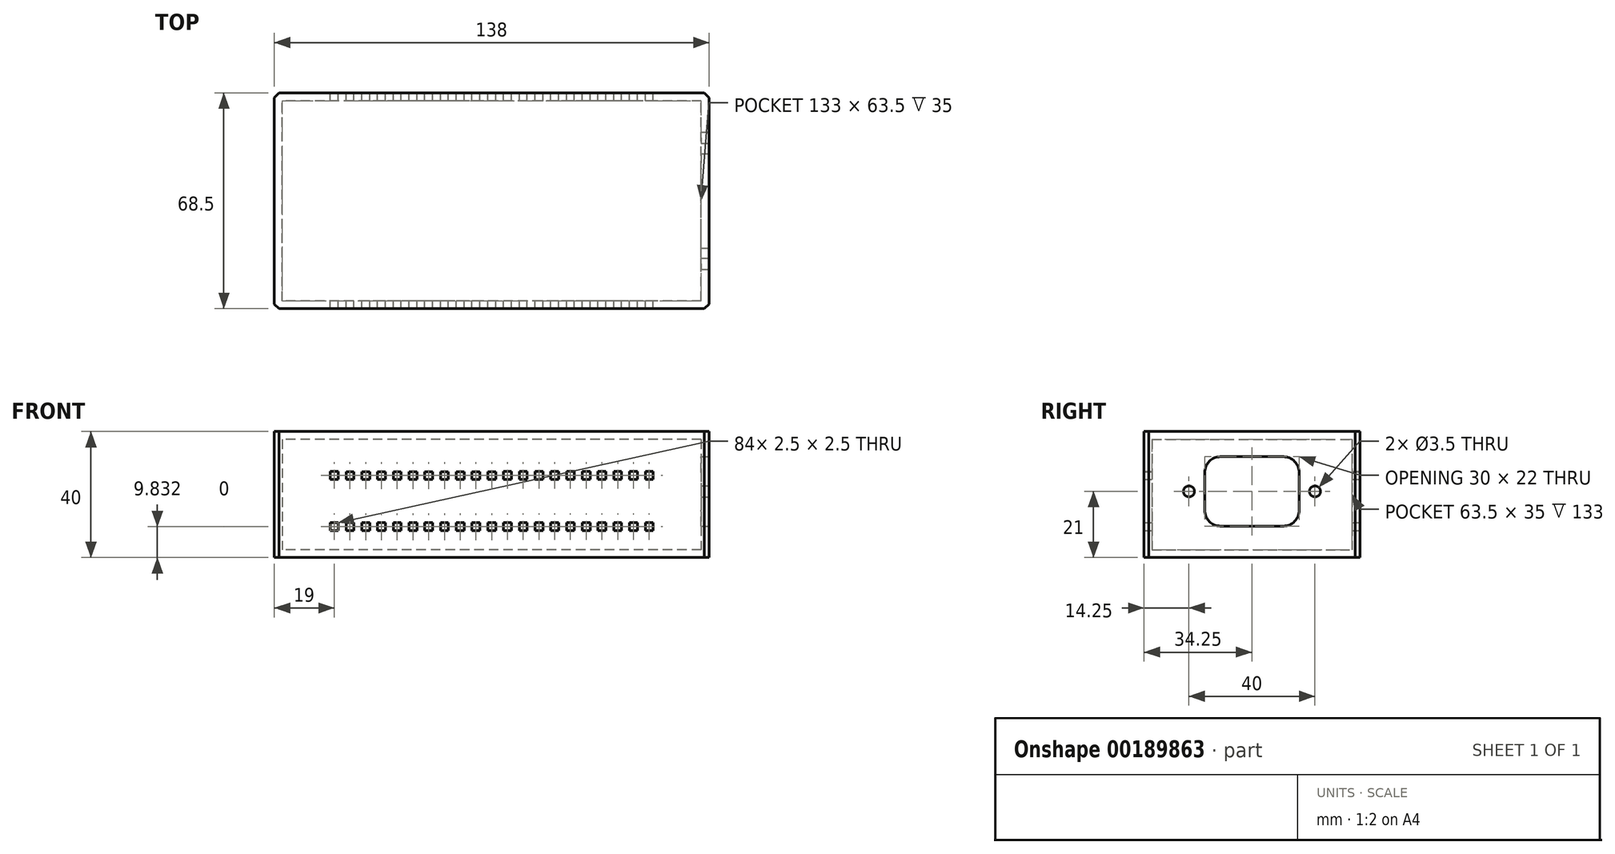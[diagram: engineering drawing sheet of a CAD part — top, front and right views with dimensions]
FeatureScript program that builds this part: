
annotation { "Feature Type Name" : "Feature", "Feature Type Description" : "" }
export const myFeature = defineFeature(function(context is Context, id is Id, definition is map)
    precondition{}
    {
        {
            var Q0;
            Q0=qCreatedBy(makeId("Top.planeOp"),FACE);
            var sketch = newSketch(context, id + "F0", { "sketchPlane" : qUnion([Q0])});
            skLineSegment(sketch, "E0.bottom", {"start": v(69, -34.25) * mm, "end": v(-69, -34.25) * mm});
            skLineSegment(sketch, "E0.top", {"start": v(69, 34.25) * mm, "end": v(-69, 34.25) * mm});
            skLineSegment(sketch, "E0.left", {"start": v(69, -34.25) * mm, "end": v(69, 34.25) * mm});
            skLineSegment(sketch, "E0.right", {"start": v(-69, -34.25) * mm, "end": v(-69, 34.25) * mm});
            skPoint(sketch, "E0.middle", {"position": v(0, 0) * mm});
            skSolve(sketch);
        }
        {
            var Q0;
            Q0 = qSketchRegion(id + "F0", true);
            extrude(context, id + "F1", {"entities" : qUnion([Q0]), "depth" : 40 * mm});
        }
        {
            var Q0;
            Q0=makeQuery(id+"F1.opExtrude","CAP_FACE",FACE,{"disambiguationData":[OSD([sQuery(id+"F0.wireOp",EDGE,"E0.bottom"),sQuery(id+"F0.wireOp",EDGE,"E0.top"),sQuery(id+"F0.wireOp",EDGE,"E0.left"),sQuery(id+"F0.wireOp",EDGE,"E0.right")])],"isStart":false});
            var Q1;
            Q1=makeQuery(id+"F1.opExtrude","SWEPT_BODY",BODY,{"disambiguationData":[OSD([sQuery(id+"F0.wireOp",EDGE,"E0.bottom"),sQuery(id+"F0.wireOp",EDGE,"E0.top"),sQuery(id+"F0.wireOp",EDGE,"E0.left"),sQuery(id+"F0.wireOp",EDGE,"E0.right")])]});
            shell(context, id + "F2", {"isHollow" : true, "entities" : qUnion([Q0]), "parts" : qUnion([Q1]), "thickness" : 2.5 * mm});
        }
        {
            var Q0;
            Q0=makeQuery(id+"F1.opExtrude","SWEPT_EDGE",EDGE,{"disambiguationData":[OSD([sQuery(id+"F0.wireOp",EDGE,"E0.top"),sQuery(id+"F0.wireOp",EDGE,"E0.right")])]});
            var Q1;
            Q1=makeQuery(id+"F1.opExtrude","SWEPT_EDGE",EDGE,{"disambiguationData":[OSD([sQuery(id+"F0.wireOp",EDGE,"E0.bottom"),sQuery(id+"F0.wireOp",EDGE,"E0.right")])]});
            var Q2;
            Q2=makeQuery(id+"F1.opExtrude","SWEPT_EDGE",EDGE,{"disambiguationData":[OSD([sQuery(id+"F0.wireOp",EDGE,"E0.top"),sQuery(id+"F0.wireOp",EDGE,"E0.left")])]});
            var Q3;
            Q3=makeQuery(id+"F1.opExtrude","SWEPT_EDGE",EDGE,{"disambiguationData":[OSD([sQuery(id+"F0.wireOp",EDGE,"E0.bottom"),sQuery(id+"F0.wireOp",EDGE,"E0.left")])]});
            chamfer(context, id + "F3", {"entities" : qUnion([Q0, Q1, Q2, Q3]), "width" : 1.5 * mm, "tangentPropagation" : true});
        }
        {
            var Q0;
            Q0=makeQuery(id+"F1.opExtrude","SWEPT_FACE",FACE,{"disambiguationData":[OSD([sQuery(id+"F0.wireOp",EDGE,"E0.left")])]});
            var sketch = newSketch(context, id + "F4", { "sketchPlane" : qUnion([Q0])});
            skLineSegment(sketch, "E1.bottom", {"start": v(15, 10) * mm, "end": v(-15, 10) * mm});
            skLineSegment(sketch, "E1.top", {"start": v(15, 32) * mm, "end": v(-15, 32) * mm});
            skLineSegment(sketch, "E1.left", {"start": v(15, 10) * mm, "end": v(15, 32) * mm});
            skLineSegment(sketch, "E1.right", {"start": v(-15, 10) * mm, "end": v(-15, 32) * mm});
            skPoint(sketch, "E1.middle", {"position": v(0, 21) * mm});
            skCircle(sketch, "E2", {"center": v(-20, 21) * mm, "radius": 1.75 * mm});
            skCircle(sketch, "E3", {"center": v(20, 21) * mm, "radius": 1.75 * mm});
            skSolve(sketch);
        }
        {
            var Q0;
            Q0 = qSketchRegion(id + "F4", true);
            extrude(context, id + "F5", {"entities" : qUnion([Q0]), "operationType" : NewBodyOperationType.REMOVE, "oppositeDirection" : true, "depth" : 25 * mm});
        }
        {
            var Q0;
            Q0=makeQuery(id+"F5.boolean.opBoolean","COPY",EDGE,{"derivedFrom":makeQuery(id+"F5.opExtrude","SWEPT_EDGE",EDGE,{"disambiguationData":[OSD([sQuery(id+"F4.wireOp",EDGE,"E1.bottom"),sQuery(id+"F4.wireOp",EDGE,"E1.right")])]})});
            var Q1;
            Q1=makeQuery(id+"F5.boolean.opBoolean","COPY",EDGE,{"derivedFrom":makeQuery(id+"F5.opExtrude","SWEPT_EDGE",EDGE,{"disambiguationData":[OSD([sQuery(id+"F4.wireOp",EDGE,"E1.bottom"),sQuery(id+"F4.wireOp",EDGE,"E1.left")])]})});
            var Q2;
            Q2=makeQuery(id+"F5.boolean.opBoolean","COPY",EDGE,{"derivedFrom":makeQuery(id+"F5.opExtrude","SWEPT_EDGE",EDGE,{"disambiguationData":[OSD([sQuery(id+"F4.wireOp",EDGE,"E1.top"),sQuery(id+"F4.wireOp",EDGE,"E1.left")])]})});
            var Q3;
            Q3=makeQuery(id+"F5.boolean.opBoolean","COPY",EDGE,{"derivedFrom":makeQuery(id+"F5.opExtrude","SWEPT_EDGE",EDGE,{"disambiguationData":[OSD([sQuery(id+"F4.wireOp",EDGE,"E1.top"),sQuery(id+"F4.wireOp",EDGE,"E1.right")])]})});
            fillet(context, id + "F6", {"entities" : qUnion([Q0, Q1, Q2, Q3]), "radius" : 5 * mm, "tangentPropagation" : true, "allowEdgeOverflow" : false});
        }
        {
            var Q0;
            Q0=makeQuery(id+"F1.opExtrude","SWEPT_FACE",FACE,{"disambiguationData":[OSD([sQuery(id+"F0.wireOp",EDGE,"E0.top")])]});
            var sketch = newSketch(context, id + "F7", { "sketchPlane" : qUnion([Q0])});
            skLineSegment(sketch, "E4.bottom", {"start": v(1.25, 24.8) * mm, "end": v(-1.25, 24.8) * mm});
            skLineSegment(sketch, "E4.top", {"start": v(1.25, 27.3) * mm, "end": v(-1.25, 27.3) * mm});
            skLineSegment(sketch, "E4.left", {"start": v(1.25, 24.8) * mm, "end": v(1.25, 27.3) * mm});
            skLineSegment(sketch, "E4.right", {"start": v(-1.25, 24.8) * mm, "end": v(-1.25, 27.3) * mm});
            skPoint(sketch, "E4.middle", {"position": v(0, 26.04) * mm});
            skLineSegment(sketch, "E5.1.0.0", {"start": v(6.25, 27.3) * mm, "end": v(3.75, 27.3) * mm});
            skLineSegment(sketch, "E5.1.0.1", {"start": v(3.75, 24.8) * mm, "end": v(3.75, 27.3) * mm});
            skPoint(sketch, "E5.1.0.2", {"position": v(5, 26.04) * mm});
            skLineSegment(sketch, "E5.1.0.3", {"start": v(6.25, 24.8) * mm, "end": v(6.25, 27.3) * mm});
            skLineSegment(sketch, "E5.1.0.4", {"start": v(6.25, 24.8) * mm, "end": v(3.75, 24.8) * mm});
            skLineSegment(sketch, "E5.2.0.0", {"start": v(11.25, 27.3) * mm, "end": v(8.75, 27.3) * mm});
            skLineSegment(sketch, "E5.2.0.1", {"start": v(8.75, 24.8) * mm, "end": v(8.75, 27.3) * mm});
            skPoint(sketch, "E5.2.0.2", {"position": v(10, 26.04) * mm});
            skLineSegment(sketch, "E5.2.0.3", {"start": v(11.25, 24.8) * mm, "end": v(11.25, 27.3) * mm});
            skLineSegment(sketch, "E5.2.0.4", {"start": v(11.25, 24.8) * mm, "end": v(8.75, 24.8) * mm});
            skLineSegment(sketch, "E5.3.0.0", {"start": v(16.25, 27.3) * mm, "end": v(13.75, 27.3) * mm});
            skLineSegment(sketch, "E5.3.0.1", {"start": v(13.75, 24.8) * mm, "end": v(13.75, 27.3) * mm});
            skPoint(sketch, "E5.3.0.2", {"position": v(15, 26.04) * mm});
            skLineSegment(sketch, "E5.3.0.3", {"start": v(16.25, 24.8) * mm, "end": v(16.25, 27.3) * mm});
            skLineSegment(sketch, "E5.3.0.4", {"start": v(16.25, 24.8) * mm, "end": v(13.75, 24.8) * mm});
            skLineSegment(sketch, "E5.4.0.0", {"start": v(21.25, 27.3) * mm, "end": v(18.75, 27.3) * mm});
            skLineSegment(sketch, "E5.4.0.1", {"start": v(18.75, 24.8) * mm, "end": v(18.75, 27.3) * mm});
            skPoint(sketch, "E5.4.0.2", {"position": v(20, 26.04) * mm});
            skLineSegment(sketch, "E5.4.0.3", {"start": v(21.25, 24.8) * mm, "end": v(21.25, 27.3) * mm});
            skLineSegment(sketch, "E5.4.0.4", {"start": v(21.25, 24.8) * mm, "end": v(18.75, 24.8) * mm});
            skLineSegment(sketch, "E5.5.0.0", {"start": v(26.25, 27.3) * mm, "end": v(23.75, 27.3) * mm});
            skLineSegment(sketch, "E5.5.0.1", {"start": v(23.75, 24.8) * mm, "end": v(23.75, 27.3) * mm});
            skPoint(sketch, "E5.5.0.2", {"position": v(25, 26.04) * mm});
            skLineSegment(sketch, "E5.5.0.3", {"start": v(26.25, 24.8) * mm, "end": v(26.25, 27.3) * mm});
            skLineSegment(sketch, "E5.5.0.4", {"start": v(26.25, 24.8) * mm, "end": v(23.75, 24.8) * mm});
            skLineSegment(sketch, "E5.6.0.0", {"start": v(31.25, 27.3) * mm, "end": v(28.75, 27.3) * mm});
            skLineSegment(sketch, "E5.6.0.1", {"start": v(28.75, 24.8) * mm, "end": v(28.75, 27.3) * mm});
            skPoint(sketch, "E5.6.0.2", {"position": v(30, 26.04) * mm});
            skLineSegment(sketch, "E5.6.0.3", {"start": v(31.25, 24.8) * mm, "end": v(31.25, 27.3) * mm});
            skLineSegment(sketch, "E5.6.0.4", {"start": v(31.25, 24.8) * mm, "end": v(28.75, 24.8) * mm});
            skLineSegment(sketch, "E5.7.0.0", {"start": v(36.25, 27.3) * mm, "end": v(33.75, 27.3) * mm});
            skLineSegment(sketch, "E5.7.0.1", {"start": v(33.75, 24.8) * mm, "end": v(33.75, 27.3) * mm});
            skPoint(sketch, "E5.7.0.2", {"position": v(35, 26.04) * mm});
            skLineSegment(sketch, "E5.7.0.3", {"start": v(36.25, 24.8) * mm, "end": v(36.25, 27.3) * mm});
            skLineSegment(sketch, "E5.7.0.4", {"start": v(36.25, 24.8) * mm, "end": v(33.75, 24.8) * mm});
            skLineSegment(sketch, "E5.8.0.0", {"start": v(41.25, 27.3) * mm, "end": v(38.75, 27.3) * mm});
            skLineSegment(sketch, "E5.8.0.1", {"start": v(38.75, 24.8) * mm, "end": v(38.75, 27.3) * mm});
            skPoint(sketch, "E5.8.0.2", {"position": v(40, 26.04) * mm});
            skLineSegment(sketch, "E5.8.0.3", {"start": v(41.25, 24.8) * mm, "end": v(41.25, 27.3) * mm});
            skLineSegment(sketch, "E5.8.0.4", {"start": v(41.25, 24.8) * mm, "end": v(38.75, 24.8) * mm});
            skLineSegment(sketch, "E5.9.0.0", {"start": v(46.25, 27.3) * mm, "end": v(43.75, 27.3) * mm});
            skLineSegment(sketch, "E5.9.0.1", {"start": v(43.75, 24.8) * mm, "end": v(43.75, 27.3) * mm});
            skPoint(sketch, "E5.9.0.2", {"position": v(45, 26.04) * mm});
            skLineSegment(sketch, "E5.9.0.3", {"start": v(46.25, 24.8) * mm, "end": v(46.25, 27.3) * mm});
            skLineSegment(sketch, "E5.9.0.4", {"start": v(46.25, 24.8) * mm, "end": v(43.75, 24.8) * mm});
            skLineSegment(sketch, "E5.direction1", {"start": v(-1.25, 24.8) * mm, "end": v(3.75, 24.8) * mm, "construction": true});
            skLineSegment(sketch, "E6.bottom", {"start": v(-48.75, 24.83) * mm, "end": v(-51.25, 24.83) * mm});
            skLineSegment(sketch, "E6.top", {"start": v(-48.75, 27.33) * mm, "end": v(-51.25, 27.33) * mm});
            skLineSegment(sketch, "E6.left", {"start": v(-48.75, 24.83) * mm, "end": v(-48.75, 27.33) * mm});
            skLineSegment(sketch, "E6.right", {"start": v(-51.25, 24.83) * mm, "end": v(-51.25, 27.33) * mm});
            skPoint(sketch, "E6.middle", {"position": v(-50, 26.08) * mm});
            skLineSegment(sketch, "E7.1.0.0", {"start": v(-43.75, 27.33) * mm, "end": v(-46.25, 27.33) * mm});
            skLineSegment(sketch, "E7.1.0.1", {"start": v(-46.25, 24.83) * mm, "end": v(-46.25, 27.33) * mm});
            skPoint(sketch, "E7.1.0.2", {"position": v(-45, 26.08) * mm});
            skLineSegment(sketch, "E7.1.0.3", {"start": v(-43.75, 24.83) * mm, "end": v(-43.75, 27.33) * mm});
            skLineSegment(sketch, "E7.1.0.4", {"start": v(-43.75, 24.83) * mm, "end": v(-46.25, 24.83) * mm});
            skLineSegment(sketch, "E7.2.0.0", {"start": v(-38.75, 27.33) * mm, "end": v(-41.25, 27.33) * mm});
            skLineSegment(sketch, "E7.2.0.1", {"start": v(-41.25, 24.83) * mm, "end": v(-41.25, 27.33) * mm});
            skPoint(sketch, "E7.2.0.2", {"position": v(-40, 26.08) * mm});
            skLineSegment(sketch, "E7.2.0.3", {"start": v(-38.75, 24.83) * mm, "end": v(-38.75, 27.33) * mm});
            skLineSegment(sketch, "E7.2.0.4", {"start": v(-38.75, 24.83) * mm, "end": v(-41.25, 24.83) * mm});
            skLineSegment(sketch, "E7.3.0.0", {"start": v(-33.75, 27.33) * mm, "end": v(-36.25, 27.33) * mm});
            skLineSegment(sketch, "E7.3.0.1", {"start": v(-36.25, 24.83) * mm, "end": v(-36.25, 27.33) * mm});
            skPoint(sketch, "E7.3.0.2", {"position": v(-35, 26.08) * mm});
            skLineSegment(sketch, "E7.3.0.3", {"start": v(-33.75, 24.83) * mm, "end": v(-33.75, 27.33) * mm});
            skLineSegment(sketch, "E7.3.0.4", {"start": v(-33.75, 24.83) * mm, "end": v(-36.25, 24.83) * mm});
            skLineSegment(sketch, "E7.4.0.0", {"start": v(-28.75, 27.33) * mm, "end": v(-31.25, 27.33) * mm});
            skLineSegment(sketch, "E7.4.0.1", {"start": v(-31.25, 24.83) * mm, "end": v(-31.25, 27.33) * mm});
            skPoint(sketch, "E7.4.0.2", {"position": v(-30, 26.08) * mm});
            skLineSegment(sketch, "E7.4.0.3", {"start": v(-28.75, 24.83) * mm, "end": v(-28.75, 27.33) * mm});
            skLineSegment(sketch, "E7.4.0.4", {"start": v(-28.75, 24.83) * mm, "end": v(-31.25, 24.83) * mm});
            skLineSegment(sketch, "E7.5.0.0", {"start": v(-23.75, 27.33) * mm, "end": v(-26.25, 27.33) * mm});
            skLineSegment(sketch, "E7.5.0.1", {"start": v(-26.25, 24.83) * mm, "end": v(-26.25, 27.33) * mm});
            skPoint(sketch, "E7.5.0.2", {"position": v(-25, 26.08) * mm});
            skLineSegment(sketch, "E7.5.0.3", {"start": v(-23.75, 24.83) * mm, "end": v(-23.75, 27.33) * mm});
            skLineSegment(sketch, "E7.5.0.4", {"start": v(-23.75, 24.83) * mm, "end": v(-26.25, 24.83) * mm});
            skLineSegment(sketch, "E7.6.0.0", {"start": v(-18.75, 27.33) * mm, "end": v(-21.25, 27.33) * mm});
            skLineSegment(sketch, "E7.6.0.1", {"start": v(-21.25, 24.83) * mm, "end": v(-21.25, 27.33) * mm});
            skPoint(sketch, "E7.6.0.2", {"position": v(-20, 26.08) * mm});
            skLineSegment(sketch, "E7.6.0.3", {"start": v(-18.75, 24.83) * mm, "end": v(-18.75, 27.33) * mm});
            skLineSegment(sketch, "E7.6.0.4", {"start": v(-18.75, 24.83) * mm, "end": v(-21.25, 24.83) * mm});
            skLineSegment(sketch, "E7.7.0.0", {"start": v(-13.75, 27.33) * mm, "end": v(-16.25, 27.33) * mm});
            skLineSegment(sketch, "E7.7.0.1", {"start": v(-16.25, 24.83) * mm, "end": v(-16.25, 27.33) * mm});
            skPoint(sketch, "E7.7.0.2", {"position": v(-15, 26.08) * mm});
            skLineSegment(sketch, "E7.7.0.3", {"start": v(-13.75, 24.83) * mm, "end": v(-13.75, 27.33) * mm});
            skLineSegment(sketch, "E7.7.0.4", {"start": v(-13.75, 24.83) * mm, "end": v(-16.25, 24.83) * mm});
            skLineSegment(sketch, "E7.8.0.0", {"start": v(-8.75, 27.33) * mm, "end": v(-11.25, 27.33) * mm});
            skLineSegment(sketch, "E7.8.0.1", {"start": v(-11.25, 24.83) * mm, "end": v(-11.25, 27.33) * mm});
            skPoint(sketch, "E7.8.0.2", {"position": v(-10, 26.08) * mm});
            skLineSegment(sketch, "E7.8.0.3", {"start": v(-8.75, 24.83) * mm, "end": v(-8.75, 27.33) * mm});
            skLineSegment(sketch, "E7.8.0.4", {"start": v(-8.75, 24.83) * mm, "end": v(-11.25, 24.83) * mm});
            skLineSegment(sketch, "E7.9.0.0", {"start": v(-3.75, 27.33) * mm, "end": v(-6.25, 27.33) * mm});
            skLineSegment(sketch, "E7.9.0.1", {"start": v(-6.25, 24.83) * mm, "end": v(-6.25, 27.33) * mm});
            skPoint(sketch, "E7.9.0.2", {"position": v(-5, 26.08) * mm});
            skLineSegment(sketch, "E7.9.0.3", {"start": v(-3.75, 24.83) * mm, "end": v(-3.75, 27.33) * mm});
            skLineSegment(sketch, "E7.9.0.4", {"start": v(-3.75, 24.83) * mm, "end": v(-6.25, 24.83) * mm});
            skLineSegment(sketch, "E7.direction1", {"start": v(-51.25, 24.83) * mm, "end": v(-46.25, 24.83) * mm, "construction": true});
            skLineSegment(sketch, "E8.9.0.0", {"start": v(51.25, 27.33) * mm, "end": v(48.75, 27.33) * mm});
            skLineSegment(sketch, "E8.9.0.1", {"start": v(48.75, 24.83) * mm, "end": v(48.75, 27.33) * mm});
            skPoint(sketch, "E8.9.0.2", {"position": v(50, 26.08) * mm});
            skLineSegment(sketch, "E8.9.0.3", {"start": v(51.25, 24.83) * mm, "end": v(51.25, 27.33) * mm});
            skLineSegment(sketch, "E8.9.0.4", {"start": v(51.25, 24.83) * mm, "end": v(48.75, 24.83) * mm});
            skLineSegment(sketch, "E9.bottom", {"start": v(1.25, 8.54) * mm, "end": v(-1.25, 8.54) * mm});
            skLineSegment(sketch, "E9.top", {"start": v(1.25, 11.04) * mm, "end": v(-1.25, 11.04) * mm});
            skLineSegment(sketch, "E9.left", {"start": v(1.25, 8.54) * mm, "end": v(1.25, 11.04) * mm});
            skLineSegment(sketch, "E9.right", {"start": v(-1.25, 8.54) * mm, "end": v(-1.25, 11.04) * mm});
            skPoint(sketch, "E9.middle", {"position": v(0, 9.8) * mm});
            skLineSegment(sketch, "E10.1.0.0", {"start": v(6.25, 11.04) * mm, "end": v(3.75, 11.04) * mm});
            skLineSegment(sketch, "E10.1.0.1", {"start": v(3.75, 8.54) * mm, "end": v(3.75, 11.04) * mm});
            skPoint(sketch, "E10.1.0.2", {"position": v(5, 9.8) * mm});
            skLineSegment(sketch, "E10.1.0.3", {"start": v(6.25, 8.54) * mm, "end": v(6.25, 11.04) * mm});
            skLineSegment(sketch, "E10.1.0.4", {"start": v(6.25, 8.54) * mm, "end": v(3.75, 8.54) * mm});
            skLineSegment(sketch, "E10.2.0.0", {"start": v(11.25, 11.04) * mm, "end": v(8.75, 11.04) * mm});
            skLineSegment(sketch, "E10.2.0.1", {"start": v(8.75, 8.54) * mm, "end": v(8.75, 11.04) * mm});
            skPoint(sketch, "E10.2.0.2", {"position": v(10, 9.8) * mm});
            skLineSegment(sketch, "E10.2.0.3", {"start": v(11.25, 8.54) * mm, "end": v(11.25, 11.04) * mm});
            skLineSegment(sketch, "E10.2.0.4", {"start": v(11.25, 8.54) * mm, "end": v(8.75, 8.54) * mm});
            skLineSegment(sketch, "E10.3.0.0", {"start": v(16.25, 11.04) * mm, "end": v(13.75, 11.04) * mm});
            skLineSegment(sketch, "E10.3.0.1", {"start": v(13.75, 8.54) * mm, "end": v(13.75, 11.04) * mm});
            skPoint(sketch, "E10.3.0.2", {"position": v(15, 9.8) * mm});
            skLineSegment(sketch, "E10.3.0.3", {"start": v(16.25, 8.54) * mm, "end": v(16.25, 11.04) * mm});
            skLineSegment(sketch, "E10.3.0.4", {"start": v(16.25, 8.54) * mm, "end": v(13.75, 8.54) * mm});
            skLineSegment(sketch, "E10.4.0.0", {"start": v(21.25, 11.04) * mm, "end": v(18.75, 11.04) * mm});
            skLineSegment(sketch, "E10.4.0.1", {"start": v(18.75, 8.54) * mm, "end": v(18.75, 11.04) * mm});
            skPoint(sketch, "E10.4.0.2", {"position": v(20, 9.8) * mm});
            skLineSegment(sketch, "E10.4.0.3", {"start": v(21.25, 8.54) * mm, "end": v(21.25, 11.04) * mm});
            skLineSegment(sketch, "E10.4.0.4", {"start": v(21.25, 8.54) * mm, "end": v(18.75, 8.54) * mm});
            skLineSegment(sketch, "E10.5.0.0", {"start": v(26.25, 11.04) * mm, "end": v(23.75, 11.04) * mm});
            skLineSegment(sketch, "E10.5.0.1", {"start": v(23.75, 8.54) * mm, "end": v(23.75, 11.04) * mm});
            skPoint(sketch, "E10.5.0.2", {"position": v(25, 9.8) * mm});
            skLineSegment(sketch, "E10.5.0.3", {"start": v(26.25, 8.54) * mm, "end": v(26.25, 11.04) * mm});
            skLineSegment(sketch, "E10.5.0.4", {"start": v(26.25, 8.54) * mm, "end": v(23.75, 8.54) * mm});
            skLineSegment(sketch, "E10.6.0.0", {"start": v(31.25, 11.04) * mm, "end": v(28.75, 11.04) * mm});
            skLineSegment(sketch, "E10.6.0.1", {"start": v(28.75, 8.54) * mm, "end": v(28.75, 11.04) * mm});
            skPoint(sketch, "E10.6.0.2", {"position": v(30, 9.8) * mm});
            skLineSegment(sketch, "E10.6.0.3", {"start": v(31.25, 8.54) * mm, "end": v(31.25, 11.04) * mm});
            skLineSegment(sketch, "E10.6.0.4", {"start": v(31.25, 8.54) * mm, "end": v(28.75, 8.54) * mm});
            skLineSegment(sketch, "E10.7.0.0", {"start": v(36.25, 11.04) * mm, "end": v(33.75, 11.04) * mm});
            skLineSegment(sketch, "E10.7.0.1", {"start": v(33.75, 8.54) * mm, "end": v(33.75, 11.04) * mm});
            skPoint(sketch, "E10.7.0.2", {"position": v(35, 9.8) * mm});
            skLineSegment(sketch, "E10.7.0.3", {"start": v(36.25, 8.54) * mm, "end": v(36.25, 11.04) * mm});
            skLineSegment(sketch, "E10.7.0.4", {"start": v(36.25, 8.54) * mm, "end": v(33.75, 8.54) * mm});
            skLineSegment(sketch, "E10.8.0.0", {"start": v(41.25, 11.04) * mm, "end": v(38.75, 11.04) * mm});
            skLineSegment(sketch, "E10.8.0.1", {"start": v(38.75, 8.54) * mm, "end": v(38.75, 11.04) * mm});
            skPoint(sketch, "E10.8.0.2", {"position": v(40, 9.8) * mm});
            skLineSegment(sketch, "E10.8.0.3", {"start": v(41.25, 8.54) * mm, "end": v(41.25, 11.04) * mm});
            skLineSegment(sketch, "E10.8.0.4", {"start": v(41.25, 8.54) * mm, "end": v(38.75, 8.54) * mm});
            skLineSegment(sketch, "E10.9.0.0", {"start": v(46.25, 11.04) * mm, "end": v(43.75, 11.04) * mm});
            skLineSegment(sketch, "E10.9.0.1", {"start": v(43.75, 8.54) * mm, "end": v(43.75, 11.04) * mm});
            skPoint(sketch, "E10.9.0.2", {"position": v(45, 9.8) * mm});
            skLineSegment(sketch, "E10.9.0.3", {"start": v(46.25, 8.54) * mm, "end": v(46.25, 11.04) * mm});
            skLineSegment(sketch, "E10.9.0.4", {"start": v(46.25, 8.54) * mm, "end": v(43.75, 8.54) * mm});
            skLineSegment(sketch, "E10.direction1", {"start": v(-1.25, 8.54) * mm, "end": v(3.75, 8.54) * mm, "construction": true});
            skLineSegment(sketch, "E11.bottom", {"start": v(-48.75, 8.58) * mm, "end": v(-51.25, 8.58) * mm});
            skLineSegment(sketch, "E11.top", {"start": v(-48.75, 11.08) * mm, "end": v(-51.25, 11.08) * mm});
            skLineSegment(sketch, "E11.left", {"start": v(-48.75, 8.58) * mm, "end": v(-48.75, 11.08) * mm});
            skLineSegment(sketch, "E11.right", {"start": v(-51.25, 8.58) * mm, "end": v(-51.25, 11.08) * mm});
            skPoint(sketch, "E11.middle", {"position": v(-50, 9.83) * mm});
            skLineSegment(sketch, "E12.1.0.0", {"start": v(-43.75, 11.08) * mm, "end": v(-46.25, 11.08) * mm});
            skLineSegment(sketch, "E12.1.0.1", {"start": v(-46.25, 8.58) * mm, "end": v(-46.25, 11.08) * mm});
            skPoint(sketch, "E12.1.0.2", {"position": v(-45, 9.83) * mm});
            skLineSegment(sketch, "E12.1.0.3", {"start": v(-43.75, 8.58) * mm, "end": v(-43.75, 11.08) * mm});
            skLineSegment(sketch, "E12.1.0.4", {"start": v(-43.75, 8.58) * mm, "end": v(-46.25, 8.58) * mm});
            skLineSegment(sketch, "E12.2.0.0", {"start": v(-38.75, 11.08) * mm, "end": v(-41.25, 11.08) * mm});
            skLineSegment(sketch, "E12.2.0.1", {"start": v(-41.25, 8.58) * mm, "end": v(-41.25, 11.08) * mm});
            skPoint(sketch, "E12.2.0.2", {"position": v(-40, 9.83) * mm});
            skLineSegment(sketch, "E12.2.0.3", {"start": v(-38.75, 8.58) * mm, "end": v(-38.75, 11.08) * mm});
            skLineSegment(sketch, "E12.2.0.4", {"start": v(-38.75, 8.58) * mm, "end": v(-41.25, 8.58) * mm});
            skLineSegment(sketch, "E12.3.0.0", {"start": v(-33.75, 11.08) * mm, "end": v(-36.25, 11.08) * mm});
            skLineSegment(sketch, "E12.3.0.1", {"start": v(-36.25, 8.58) * mm, "end": v(-36.25, 11.08) * mm});
            skPoint(sketch, "E12.3.0.2", {"position": v(-35, 9.83) * mm});
            skLineSegment(sketch, "E12.3.0.3", {"start": v(-33.75, 8.58) * mm, "end": v(-33.75, 11.08) * mm});
            skLineSegment(sketch, "E12.3.0.4", {"start": v(-33.75, 8.58) * mm, "end": v(-36.25, 8.58) * mm});
            skLineSegment(sketch, "E12.4.0.0", {"start": v(-28.75, 11.08) * mm, "end": v(-31.25, 11.08) * mm});
            skLineSegment(sketch, "E12.4.0.1", {"start": v(-31.25, 8.58) * mm, "end": v(-31.25, 11.08) * mm});
            skPoint(sketch, "E12.4.0.2", {"position": v(-30, 9.83) * mm});
            skLineSegment(sketch, "E12.4.0.3", {"start": v(-28.75, 8.58) * mm, "end": v(-28.75, 11.08) * mm});
            skLineSegment(sketch, "E12.4.0.4", {"start": v(-28.75, 8.58) * mm, "end": v(-31.25, 8.58) * mm});
            skLineSegment(sketch, "E12.5.0.0", {"start": v(-23.75, 11.08) * mm, "end": v(-26.25, 11.08) * mm});
            skLineSegment(sketch, "E12.5.0.1", {"start": v(-26.25, 8.58) * mm, "end": v(-26.25, 11.08) * mm});
            skPoint(sketch, "E12.5.0.2", {"position": v(-25, 9.83) * mm});
            skLineSegment(sketch, "E12.5.0.3", {"start": v(-23.75, 8.58) * mm, "end": v(-23.75, 11.08) * mm});
            skLineSegment(sketch, "E12.5.0.4", {"start": v(-23.75, 8.58) * mm, "end": v(-26.25, 8.58) * mm});
            skLineSegment(sketch, "E12.6.0.0", {"start": v(-18.75, 11.08) * mm, "end": v(-21.25, 11.08) * mm});
            skLineSegment(sketch, "E12.6.0.1", {"start": v(-21.25, 8.58) * mm, "end": v(-21.25, 11.08) * mm});
            skPoint(sketch, "E12.6.0.2", {"position": v(-20, 9.83) * mm});
            skLineSegment(sketch, "E12.6.0.3", {"start": v(-18.75, 8.58) * mm, "end": v(-18.75, 11.08) * mm});
            skLineSegment(sketch, "E12.6.0.4", {"start": v(-18.75, 8.58) * mm, "end": v(-21.25, 8.58) * mm});
            skLineSegment(sketch, "E12.7.0.0", {"start": v(-13.75, 11.08) * mm, "end": v(-16.25, 11.08) * mm});
            skLineSegment(sketch, "E12.7.0.1", {"start": v(-16.25, 8.58) * mm, "end": v(-16.25, 11.08) * mm});
            skPoint(sketch, "E12.7.0.2", {"position": v(-15, 9.83) * mm});
            skLineSegment(sketch, "E12.7.0.3", {"start": v(-13.75, 8.58) * mm, "end": v(-13.75, 11.08) * mm});
            skLineSegment(sketch, "E12.7.0.4", {"start": v(-13.75, 8.58) * mm, "end": v(-16.25, 8.58) * mm});
            skLineSegment(sketch, "E12.8.0.0", {"start": v(-8.75, 11.08) * mm, "end": v(-11.25, 11.08) * mm});
            skLineSegment(sketch, "E12.8.0.1", {"start": v(-11.25, 8.58) * mm, "end": v(-11.25, 11.08) * mm});
            skPoint(sketch, "E12.8.0.2", {"position": v(-10, 9.83) * mm});
            skLineSegment(sketch, "E12.8.0.3", {"start": v(-8.75, 8.58) * mm, "end": v(-8.75, 11.08) * mm});
            skLineSegment(sketch, "E12.8.0.4", {"start": v(-8.75, 8.58) * mm, "end": v(-11.25, 8.58) * mm});
            skLineSegment(sketch, "E12.9.0.0", {"start": v(-3.75, 11.08) * mm, "end": v(-6.25, 11.08) * mm});
            skLineSegment(sketch, "E12.9.0.1", {"start": v(-6.25, 8.58) * mm, "end": v(-6.25, 11.08) * mm});
            skPoint(sketch, "E12.9.0.2", {"position": v(-5, 9.83) * mm});
            skLineSegment(sketch, "E12.9.0.3", {"start": v(-3.75, 8.58) * mm, "end": v(-3.75, 11.08) * mm});
            skLineSegment(sketch, "E12.9.0.4", {"start": v(-3.75, 8.58) * mm, "end": v(-6.25, 8.58) * mm});
            skLineSegment(sketch, "E12.direction1", {"start": v(-51.25, 8.58) * mm, "end": v(-46.25, 8.58) * mm, "construction": true});
            skLineSegment(sketch, "E13.9.0.0", {"start": v(51.25, 11.08) * mm, "end": v(48.75, 11.08) * mm});
            skLineSegment(sketch, "E13.9.0.1", {"start": v(48.75, 8.58) * mm, "end": v(48.75, 11.08) * mm});
            skPoint(sketch, "E13.9.0.2", {"position": v(50, 9.83) * mm});
            skLineSegment(sketch, "E13.9.0.3", {"start": v(51.25, 8.58) * mm, "end": v(51.25, 11.08) * mm});
            skLineSegment(sketch, "E13.9.0.4", {"start": v(51.25, 8.58) * mm, "end": v(48.75, 8.58) * mm});
            skSolve(sketch);
        }
        {
            var Q0;
            Q0 = qSketchRegion(id + "F7", true);
            extrude(context, id + "F8", {"entities" : qUnion([Q0]), "operationType" : NewBodyOperationType.REMOVE, "oppositeDirection" : true, "depth" : 89.7 * mm});
        }
    });
